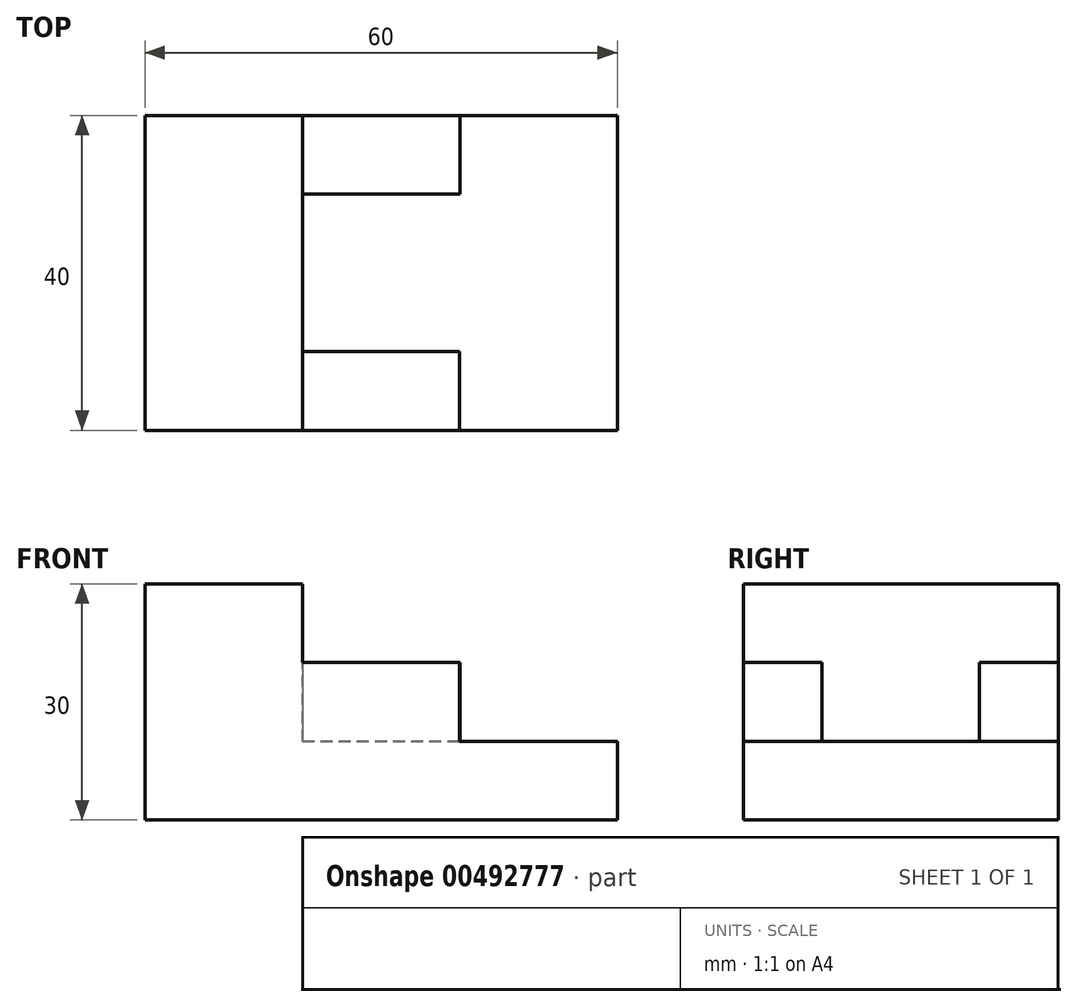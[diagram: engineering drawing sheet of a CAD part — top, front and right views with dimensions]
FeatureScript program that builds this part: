
annotation { "Feature Type Name" : "Feature", "Feature Type Description" : "" }
export const myFeature = defineFeature(function(context is Context, id is Id, definition is map)
    precondition{}
    {
        {
            var Q0;
            Q0=qCreatedBy(makeId("Top.planeOp"),FACE);
            var sketch = newSketch(context, id + "F0", { "sketchPlane" : qUnion([Q0])});
            skLineSegment(sketch, "E0", {"start": v(0, 0) * mm, "end": v(60, 0) * mm});
            skLineSegment(sketch, "E1", {"start": v(60, 0) * mm, "end": v(60, 40) * mm});
            skLineSegment(sketch, "E2", {"start": v(0, 0) * mm, "end": v(0, 40) * mm});
            skLineSegment(sketch, "E3", {"start": v(60, 40) * mm, "end": v(0, 40) * mm});
            skSolve(sketch);
        }
        {
            var Q0;
            Q0=qCreatedBy(makeId("Top.planeOp"),FACE);
            var sketch = newSketch(context, id + "F1", { "sketchPlane" : qUnion([Q0])});
            skLineSegment(sketch, "E4", {"start": v(0, 0) * mm, "end": v(20, 0) * mm});
            skLineSegment(sketch, "E5", {"start": v(20, 0) * mm, "end": v(20, 40) * mm});
            skLineSegment(sketch, "E6", {"start": v(20, 40) * mm, "end": v(0, 40) * mm});
            skLineSegment(sketch, "E7", {"start": v(0, 40) * mm, "end": v(0, 0) * mm});
            skSolve(sketch);
        }
        {
            var Q0;
            Q0=qCreatedBy(makeId("Top.planeOp"),FACE);
            var sketch = newSketch(context, id + "F2", { "sketchPlane" : qUnion([Q0])});
            skLineSegment(sketch, "E8", {"start": v(19.93, 0) * mm, "end": v(39.93, 0) * mm});
            skLineSegment(sketch, "E9", {"start": v(39.93, 0) * mm, "end": v(39.93, 10) * mm});
            skLineSegment(sketch, "E10", {"start": v(39.93, 10) * mm, "end": v(19.93, 10) * mm});
            skLineSegment(sketch, "E11", {"start": v(19.93, 10) * mm, "end": v(19.93, 0) * mm});
            skLineSegment(sketch, "E12", {"start": v(20.01, 40) * mm, "end": v(20.01, 30) * mm});
            skLineSegment(sketch, "E13", {"start": v(20.01, 30) * mm, "end": v(40.01, 30) * mm});
            skLineSegment(sketch, "E14", {"start": v(40.01, 30) * mm, "end": v(40.01, 40) * mm});
            skLineSegment(sketch, "E15", {"start": v(40.01, 40) * mm, "end": v(20.01, 40) * mm});
            skSolve(sketch);
        }
        {
            var Q0;
            Q0 = qSketchRegion(id + "F0", true);
            extrude(context, id + "F3", {"entities" : qUnion([Q0]), "depth" : 10 * mm});
        }
        {
            var Q0;
            Q0 = qSketchRegion(id + "F1", true);
            extrude(context, id + "F4", {"entities" : qUnion([Q0]), "operationType" : NewBodyOperationType.ADD, "depth" : 30 * mm});
        }
        {
            var Q0;
            Q0=makeQuery(id+"F2.imprint","IMPRINT",FACE,{"disambiguationData":[TD([[makeQuery(id+"F2.imprint","IMPRINT",EDGE,{"derivedFrom":sQuery(id+"F2.wireOp",EDGE,"E8")}),1.0]])]});
            var Q1;
            Q1=makeQuery(id+"F2.imprint","IMPRINT",FACE,{"disambiguationData":[TD([[makeQuery(id+"F2.imprint","IMPRINT",EDGE,{"derivedFrom":sQuery(id+"F2.wireOp",EDGE,"E12")}),1.0]])]});
            extrude(context, id + "F5", {"entities" : qUnion([Q0, Q1]), "operationType" : NewBodyOperationType.ADD, "depth" : 20 * mm});
        }
    });
